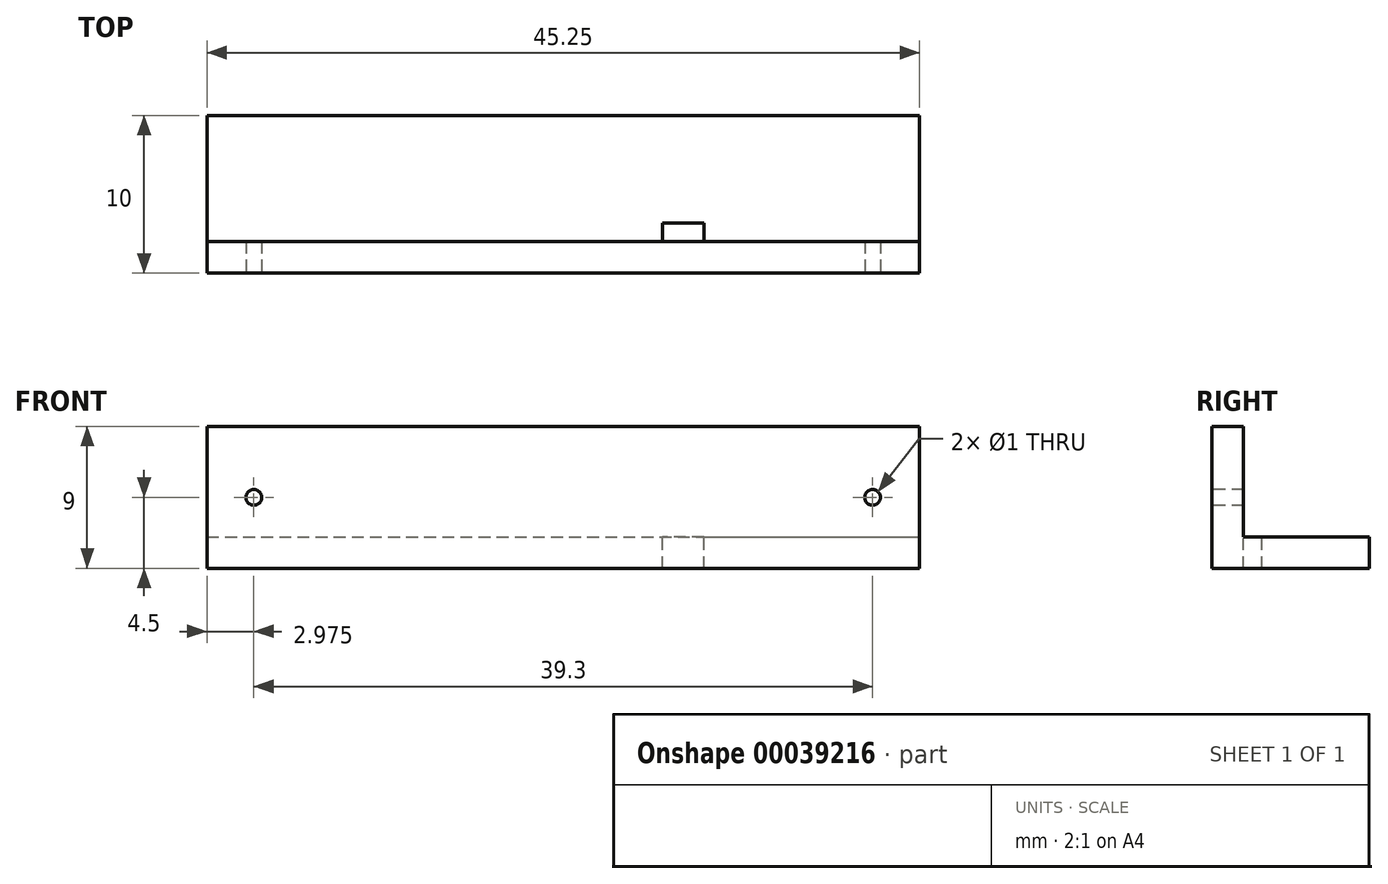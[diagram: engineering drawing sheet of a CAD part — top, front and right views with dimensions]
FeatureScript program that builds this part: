
annotation { "Feature Type Name" : "Feature", "Feature Type Description" : "" }
export const myFeature = defineFeature(function(context is Context, id is Id, definition is map)
    precondition{}
    {
        {
            var Q0;
            Q0=qCreatedBy(makeId("Top.planeOp"),FACE);
            var sketch = newSketch(context, id + "F0", { "sketchPlane" : qUnion([Q0])});
            skLineSegment(sketch, "E0.bottom", {"start": v(0, 0) * mm, "end": v(45.25, 0) * mm});
            skLineSegment(sketch, "E0.top", {"start": v(0, 10) * mm, "end": v(45.25, 10) * mm});
            skLineSegment(sketch, "E0.left", {"start": v(0, 0) * mm, "end": v(0, 10) * mm});
            skLineSegment(sketch, "E0.right", {"start": v(45.25, 0) * mm, "end": v(45.25, 10) * mm});
            skSolve(sketch);
        }
        {
            var Q0;
            Q0=makeQuery(id+"F0.imprint","IMPRINT",FACE,{"disambiguationData":[TD([[makeQuery(id+"F0.imprint","IMPRINT",EDGE,{"derivedFrom":sQuery(id+"F0.wireOp",EDGE,"E0.bottom")}),1.0]])]});
            extrude(context, id + "F1", {"entities" : qUnion([Q0]), "depth" : 2 * mm});
        }
        {
            var Q0;
            Q0=makeQuery(id+"F1.opExtrude","CAP_FACE",FACE,{"disambiguationData":[OSD([sQuery(id+"F0.wireOp",EDGE,"E0.bottom"),sQuery(id+"F0.wireOp",EDGE,"E0.top"),sQuery(id+"F0.wireOp",EDGE,"E0.left"),sQuery(id+"F0.wireOp",EDGE,"E0.right")])],"isStart":false});
            var sketch = newSketch(context, id + "F2", { "sketchPlane" : qUnion([Q0])});
            skLineSegment(sketch, "E1.bottom", {"start": v(0, 0) * mm, "end": v(45.25, 0) * mm});
            skLineSegment(sketch, "E1.top", {"start": v(0, 2) * mm, "end": v(45.25, 2) * mm});
            skLineSegment(sketch, "E1.left", {"start": v(0, 0) * mm, "end": v(0, 2) * mm});
            skLineSegment(sketch, "E1.right", {"start": v(45.25, 0) * mm, "end": v(45.25, 2) * mm});
            skSolve(sketch);
        }
        {
            var Q0;
            Q0 = qSketchRegion(id + "F2", true);
            extrude(context, id + "F3", {"entities" : qUnion([Q0]), "operationType" : NewBodyOperationType.ADD, "depth" : 7 * mm});
        }
        {
            var Q0;
            Q0=makeQuery(id+"F3.boolean.opBoolean","MERGE",FACE,{"derivedFrom":[makeQuery(id+"F1.opExtrude","SWEPT_FACE",FACE,{"disambiguationData":[OSD([sQuery(id+"F0.wireOp",EDGE,"E0.bottom")])]}),makeQuery(id+"F3.opExtrude","SWEPT_FACE",FACE,{"disambiguationData":[OSD([sQuery(id+"F2.wireOp",EDGE,"E1.bottom")])]})]});
            var sketch = newSketch(context, id + "F4", { "sketchPlane" : qUnion([Q0])});
            skCircle(sketch, "E2", {"center": v(2.97, 4.5) * mm, "radius": 0.5 * mm});
            skCircle(sketch, "E3", {"center": v(42.27, 4.5) * mm, "radius": 0.5 * mm});
            skSolve(sketch);
        }
        {
            var Q0;
            Q0=makeQuery(id+"F4.imprint","IMPRINT",FACE,{"disambiguationData":[TD([[makeQuery(id+"F4.imprint","IMPRINT",EDGE,{"derivedFrom":sQuery(id+"F4.wireOp",EDGE,"E2")}),1.0]])]});
            extrude(context, id + "F5", {"entities" : qUnion([Q0]), "operationType" : NewBodyOperationType.REMOVE, "oppositeDirection" : true, "depth" : 25 * mm});
        }
        {
            var Q0;
            Q0=makeQuery(id+"F4.imprint","IMPRINT",FACE,{"disambiguationData":[TD([[makeQuery(id+"F4.imprint","IMPRINT",EDGE,{"derivedFrom":sQuery(id+"F4.wireOp",EDGE,"E3")}),1.0]])]});
            extrude(context, id + "F6", {"entities" : qUnion([Q0]), "operationType" : NewBodyOperationType.REMOVE, "oppositeDirection" : true, "depth" : 25 * mm});
        }
        {
            var Q0;
            Q0=makeQuery(id+"F1.opExtrude","CAP_FACE",FACE,{"disambiguationData":[OSD([sQuery(id+"F0.wireOp",EDGE,"E0.bottom"),sQuery(id+"F0.wireOp",EDGE,"E0.top"),sQuery(id+"F0.wireOp",EDGE,"E0.left"),sQuery(id+"F0.wireOp",EDGE,"E0.right")])],"isStart":false});
            var sketch = newSketch(context, id + "F7", { "sketchPlane" : qUnion([Q0])});
            skLineSegment(sketch, "E4.bottom", {"start": v(31.56, 2) * mm, "end": v(28.94, 2) * mm});
            skLineSegment(sketch, "E4.top", {"start": v(31.56, 3.18) * mm, "end": v(28.94, 3.18) * mm});
            skLineSegment(sketch, "E4.left", {"start": v(31.56, 2) * mm, "end": v(31.56, 3.18) * mm});
            skLineSegment(sketch, "E4.right", {"start": v(28.94, 2) * mm, "end": v(28.94, 3.18) * mm});
            skSolve(sketch);
        }
        {
            var Q0;
            Q0=makeQuery(id+"F7.imprint","IMPRINT",FACE,{"disambiguationData":[TD([[makeQuery(id+"F7.imprint","IMPRINT",EDGE,{"derivedFrom":sQuery(id+"F7.wireOp",EDGE,"E4.bottom")}),1.0]])]});
            extrude(context, id + "F8", {"entities" : qUnion([Q0]), "operationType" : NewBodyOperationType.REMOVE, "oppositeDirection" : true, "depth" : 3 * mm});
        }
    });
